# Revit family: Sanitary_Accessories_Svedholm_Slits-RWC-handles
name_source: partatom
category: Furniture
revit_build: Autodesk Revit 2018 (Build: 20190510_1515(x64)
units: mm (PartAtom-declared; Revit-internal decimal feet)

## family parameters
Cut with Voids When Loaded = No
Host = Face
OmniClass Number = 23.21.11.00
OmniClass Title = Commercial Furniture
Room Calculation Point = No
Shared = No

## types (3) — shared parameters
BIMobject category = Accessories
Default Elevation = 1219 mm
Description = Slits RWC handles
Edition number = 1
IFC Classification = Object
Manufacturer = Svedholm
Manufacturer name = Svedholm
Model = Slits RWC handles
OmniClass Code = 23-21 11 00
OmniClass Description = Commercial Furniture
Product Guid = 1915c2d7-7e75-43ea-a592-785a7908f1c2
Product SKU = Slits-RWC-handles
Product data url = https://bimobject.com
Product family = Slits
Product group = Accessories
Product name = Slits RWC handles
Product url = https://www.svedholm.se
QR code = https://bimobject.com
URL = https://www.svedholm.se
Uniclass 2015 Code = Zz_30_60
Uniclass 2015 Name = Objects

## per-type parameters (varying)
| type | 300 mm | 450mm | 600mm |
| ART - (410.600.080) Width - (300mm) | Yes | No | No |
| ART - (410.600.081) Width - (450mm) | No | Yes | No |
| ART - (410.600.082) Width - (600mm) | No | No | Yes |

## geometry (parser evidence)
native form markers: Sweep x3
no freeform markers — native parametric forms only
